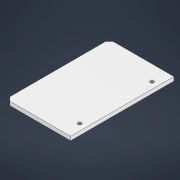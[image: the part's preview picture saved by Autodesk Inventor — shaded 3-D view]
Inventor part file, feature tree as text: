
AUTODESK INVENTOR PART (.ipt)
format: ipt  version: 2021 (Build 250183000, 183)  size: 105,984 bytes
history: native  units: mm
features: extrude x1, chamfer x1, sketch x1
ambient origin geometry x8: Origin, YZ Plane, XZ Plane, XY Plane, X Axis, Y Axis, Z Axis, Center Point
bodies: Solid1 (feature_tree)
feature tree (3):
  extrude  "Extrusion1"  Depth=3.0mm
  chamfer  "Chamfer1"  Distance=2.8mm
  sketch  "Sketch2"  dims[d2=160.0mm d3=90.0mm d4=2.8mm d5=5.0mm d6=5.0mm d8=3.0mm d9=0.0mm d10=28.0mm d11=50.0mm d12=3.0mm d13=2.0mm d14=45.0deg]
